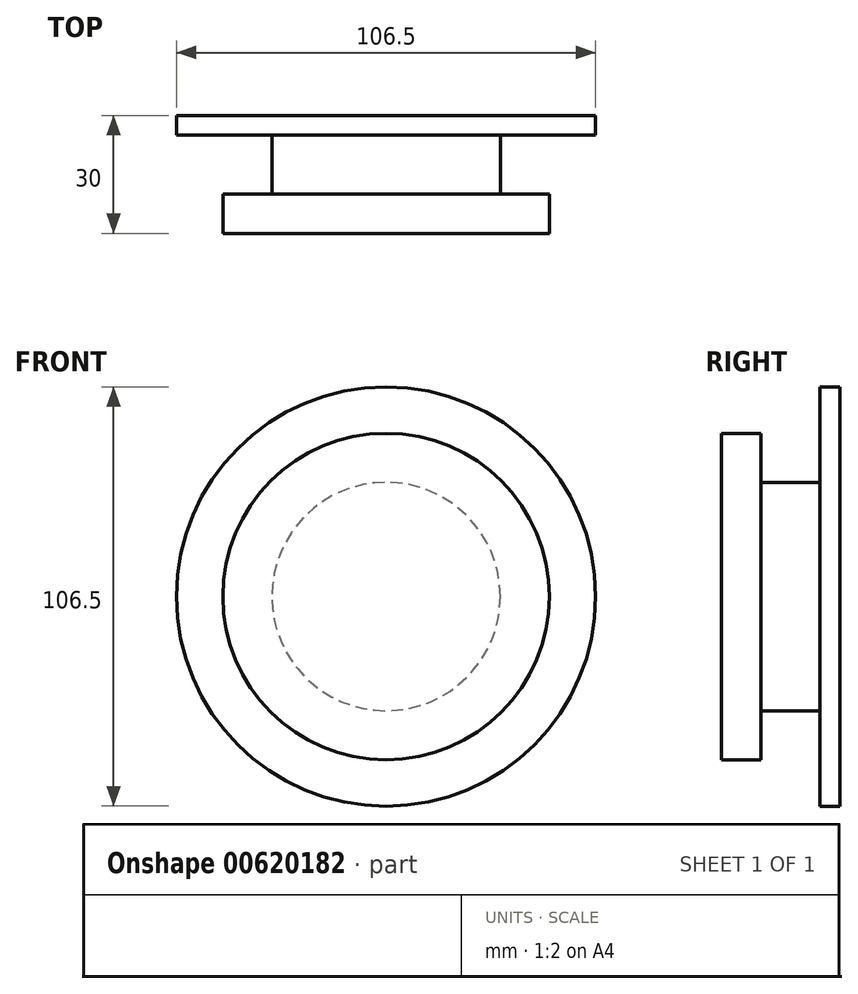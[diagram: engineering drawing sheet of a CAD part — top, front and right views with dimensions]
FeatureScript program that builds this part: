
annotation { "Feature Type Name" : "Feature", "Feature Type Description" : "" }
export const myFeature = defineFeature(function(context is Context, id is Id, definition is map)
    precondition{}
    {
        {
            var Q0;
            Q0=qCreatedBy(makeId("Front.planeOp"),FACE);
            var sketch = newSketch(context, id + "F0", { "sketchPlane" : qUnion([Q0])});
            skCircle(sketch, "E0", {"center": v(0, 0) * mm, "radius": 53.25 * mm});
            skSolve(sketch);
        }
        {
            var Q0;
            Q0 = qSketchRegion(id + "F0", true);
            extrude(context, id + "F1", {"entities" : qUnion([Q0]), "depth" : 5 * mm, "offsetDistance" : 25 * mm});
        }
        {
            var Q0;
            Q0=qCreatedBy(makeId("Front.planeOp"),FACE);
            var sketch = newSketch(context, id + "F2", { "sketchPlane" : qUnion([Q0])});
            skCircle(sketch, "E1", {"center": v(0, 0) * mm, "radius": 29.01 * mm});
            skSolve(sketch);
        }
        {
            var Q0;
            Q0 = qSketchRegion(id + "F2", true);
            extrude(context, id + "F3", {"entities" : qUnion([Q0]), "operationType" : NewBodyOperationType.ADD, "depth" : 20 * mm, "offsetDistance" : 25 * mm});
        }
        {
            var Q0;
            Q0=makeQuery(id+"F3.opExtrude","CAP_FACE",FACE,{"disambiguationData":[OSD([sQuery(id+"F2.wireOp",EDGE,"E1")])],"isStart":false});
            var sketch = newSketch(context, id + "F4", { "sketchPlane" : qUnion([Q0])});
            skCircle(sketch, "E2", {"center": v(0, 0) * mm, "radius": 41.47 * mm});
            skSolve(sketch);
        }
        {
            var Q0;
            Q0 = qSketchRegion(id + "F4", true);
            extrude(context, id + "F5", {"entities" : qUnion([Q0]), "operationType" : NewBodyOperationType.ADD, "depth" : 10 * mm, "offsetDistance" : 25 * mm});
        }
    });
